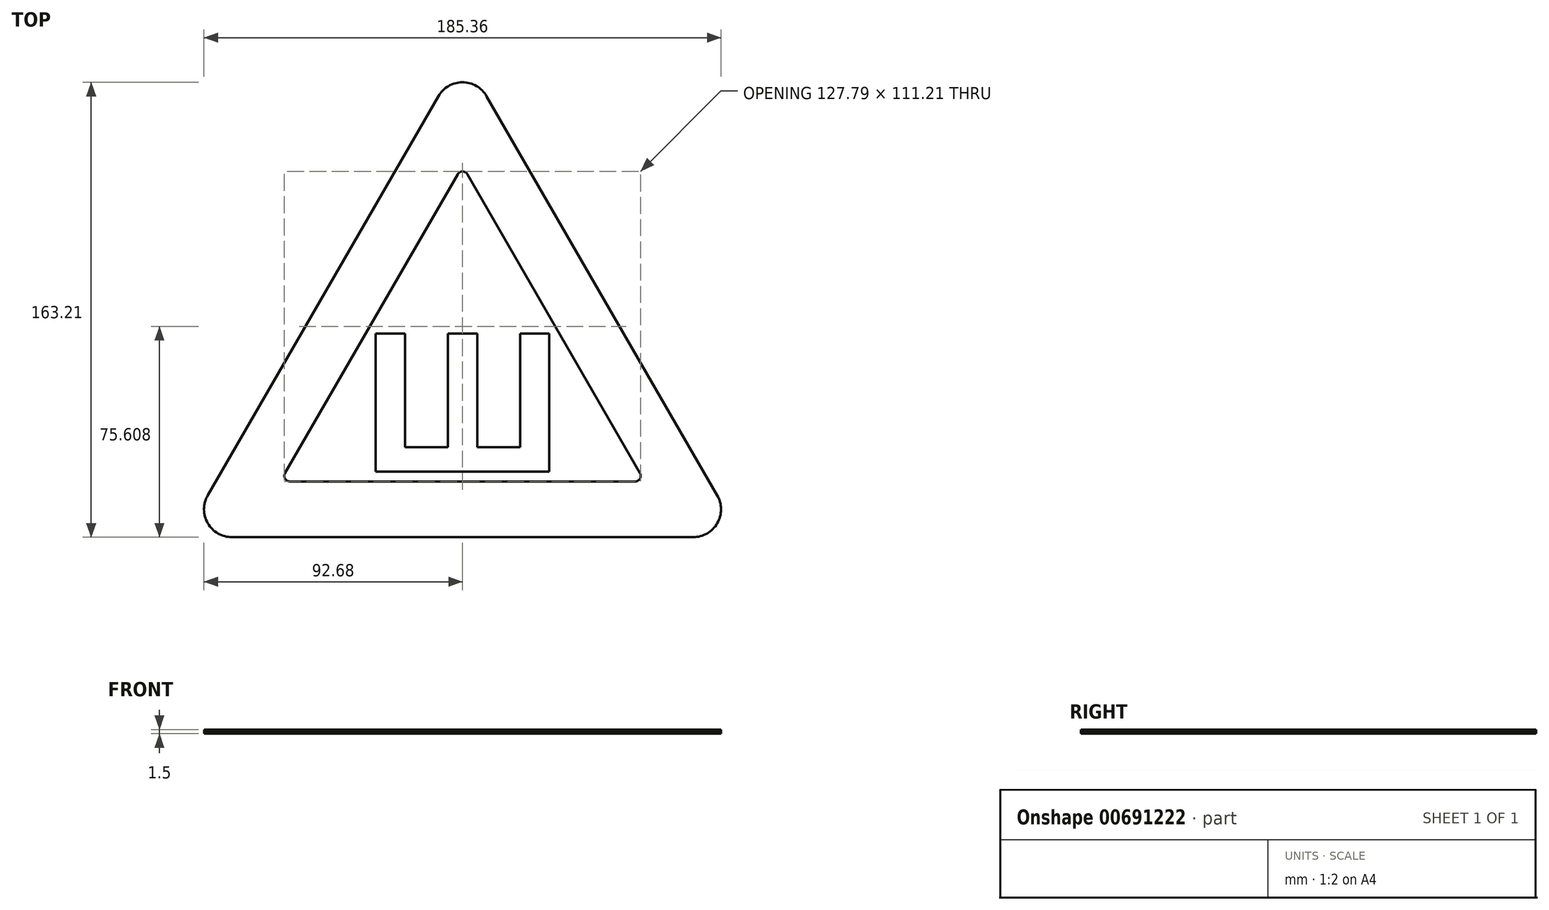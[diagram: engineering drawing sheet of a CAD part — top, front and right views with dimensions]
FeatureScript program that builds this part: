
annotation { "Feature Type Name" : "Feature", "Feature Type Description" : "" }
export const myFeature = defineFeature(function(context is Context, id is Id, definition is map)
    precondition{}
    {
        {
            var Q0;
            Q0=qCreatedBy(makeId("Top.planeOp"),FACE);
            var sketch = newSketch(context, id + "F0", { "sketchPlane" : qUnion([Q0])});
            skCircle(sketch, "E0.cCircle", {"center": v(0, 0) * mm, "radius": 57.74 * mm, "construction": true});
            skLineSegment(sketch, "E0.0", {"start": v(8.66, 100.47) * mm, "end": v(91.34, -42.74) * mm});
            skLineSegment(sketch, "E0.1", {"start": v(82.68, -57.74) * mm, "end": v(-82.68, -57.74) * mm});
            skLineSegment(sketch, "E0.2", {"start": v(-91.34, -42.74) * mm, "end": v(-8.66, 100.47) * mm});
            skPoint(sketch, "E0.0.midPoint", {"position": v(50, 28.87) * mm});
            skLineSegment(sketch, "E1.0", {"start": v(-63.63, -34.74) * mm, "end": v(-1.73, 72.47) * mm});
            skLineSegment(sketch, "E1.1", {"start": v(61.9, -37.74) * mm, "end": v(-61.9, -37.74) * mm});
            skLineSegment(sketch, "E1.2", {"start": v(1.73, 72.47) * mm, "end": v(63.63, -34.74) * mm});
            skPoint(sketch, "E2.visualSharp", {"position": v(0, 115.47) * mm});
            skArc(sketch, "E2.filletArc", {"start": v(8.66, 100.47) * mm, "mid": v(0, 105.47) * mm, "end": v(-8.66, 100.47) * mm});
            skPoint(sketch, "E3.visualSharp", {"position": v(-100, -57.74) * mm});
            skArc(sketch, "E3.filletArc", {"start": v(-91.34, -42.74) * mm, "mid": v(-91.34, -52.74) * mm, "end": v(-82.68, -57.74) * mm});
            skPoint(sketch, "E4.visualSharp", {"position": v(100, -57.74) * mm});
            skArc(sketch, "E4.filletArc", {"start": v(82.68, -57.74) * mm, "mid": v(91.34, -52.74) * mm, "end": v(91.34, -42.74) * mm});
            skPoint(sketch, "E5.visualSharp", {"position": v(0, 75.47) * mm});
            skArc(sketch, "E5.filletArc", {"start": v(1.73, 72.47) * mm, "mid": v(0, 73.47) * mm, "end": v(-1.73, 72.47) * mm});
            skPoint(sketch, "E6.visualSharp", {"position": v(65.36, -37.74) * mm});
            skArc(sketch, "E6.filletArc", {"start": v(61.9, -37.74) * mm, "mid": v(63.63, -36.74) * mm, "end": v(63.63, -34.74) * mm});
            skPoint(sketch, "E7.visualSharp", {"position": v(-65.36, -37.74) * mm});
            skArc(sketch, "E7.filletArc", {"start": v(-63.63, -34.74) * mm, "mid": v(-63.63, -36.74) * mm, "end": v(-61.9, -37.74) * mm});
            skText(sketch, "E8", { "text": "Ш", "fontName": "OpenSans-Bold.ttf"});
            const initialGuessF0  = {"E8": [-0.03734, -0.0342, 1, 0, 0.0499]};
            skSetInitialGuess(sketch, initialGuessF0);
            skSolve(sketch);
        }
        {
            var Q0;
            Q0=makeQuery(id+"F0.imprint","IMPRINT",FACE,{"disambiguationData":[TD([[makeQuery(id+"F0.imprint","IMPRINT",EDGE,{"derivedFrom":sQuery(id+"F0.wireOp",EDGE,"E1.0")}),-1.0]])]});
            var Q1;
            Q1=makeQuery(id+"F0.imprint","IMPRINT",FACE,{"disambiguationData":[TD([[makeQuery(id+"F0.imprint","IMPRINT",EDGE,{"derivedFrom":sQuery(id+"F0.wireOp",EDGE,"E8.sketch_text.stroke-0")}),-1.0]])]});
            var Q2;
            Q2=makeQuery(id+"F0.imprint","IMPRINT",FACE,{"disambiguationData":[TD([[makeQuery(id+"F0.imprint","IMPRINT",EDGE,{"derivedFrom":sQuery(id+"F0.wireOp",EDGE,"E0.0")}),-1.0]])]});
            extrude(context, id + "F1", {"entities" : qUnion([Q0, Q1, Q2]), "depth" : 0.5 * mm, "offsetDistance" : 25 * mm});
        }
        {
            var Q0;
            Q0=makeQuery(id+"F0.imprint","IMPRINT",FACE,{"disambiguationData":[TD([[makeQuery(id+"F0.imprint","IMPRINT",EDGE,{"derivedFrom":sQuery(id+"F0.wireOp",EDGE,"E0.0")}),-1.0]])]});
            var Q1;
            Q1=makeQuery(id+"F0.imprint","IMPRINT",FACE,{"disambiguationData":[TD([[makeQuery(id+"F0.imprint","IMPRINT",EDGE,{"derivedFrom":sQuery(id+"F0.wireOp",EDGE,"E1.0")}),-1.0]])]});
            extrude(context, id + "F2", {"entities" : qUnion([Q0, Q1]), "depth" : (0.5 + 0.5) * mm, "offsetDistance" : 25 * mm});
        }
        {
            var Q0;
            Q0=makeQuery(id+"F0.imprint","IMPRINT",FACE,{"disambiguationData":[TD([[makeQuery(id+"F0.imprint","IMPRINT",EDGE,{"derivedFrom":sQuery(id+"F0.wireOp",EDGE,"E0.0")}),-1.0]])]});
            extrude(context, id + "F3", {"entities" : qUnion([Q0]), "depth" : (0.5 + 0.5 + 0.5) * mm, "offsetDistance" : 25 * mm});
        }
    });
